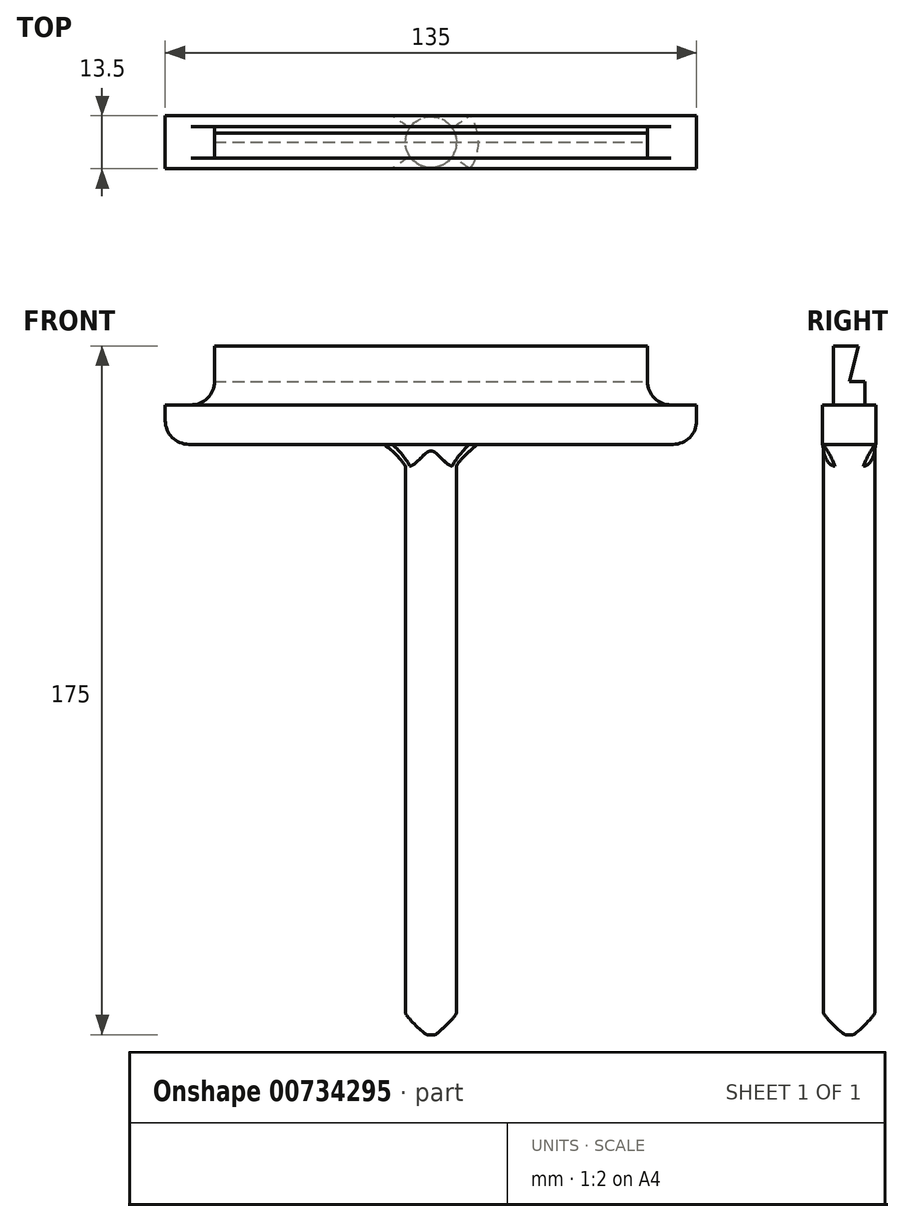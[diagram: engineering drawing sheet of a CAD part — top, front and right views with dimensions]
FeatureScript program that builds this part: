
annotation { "Feature Type Name" : "Feature", "Feature Type Description" : "" }
export const myFeature = defineFeature(function(context is Context, id is Id, definition is map)
    precondition{}
    {
        {
            var Q0;
            Q0=qCreatedBy(makeId("Top.planeOp"),FACE);
            var sketch = newSketch(context, id + "F0", { "sketchPlane" : qUnion([Q0])});
            skLineSegment(sketch, "E0.bottom", {"start": v(67.5, -6.75) * mm, "end": v(-67.5, -6.75) * mm});
            skLineSegment(sketch, "E0.top", {"start": v(67.5, 6.75) * mm, "end": v(-67.5, 6.75) * mm});
            skLineSegment(sketch, "E0.left", {"start": v(67.5, -6.75) * mm, "end": v(67.5, 6.75) * mm});
            skLineSegment(sketch, "E0.right", {"start": v(-67.5, -6.75) * mm, "end": v(-67.5, 6.75) * mm});
            skPoint(sketch, "E0.middle", {"position": v(0, 0) * mm});
            skSolve(sketch);
        }
        {
            var Q0;
            Q0 = qSketchRegion(id + "F0", true);
            extrude(context, id + "F1", {"entities" : qUnion([Q0]), "depth" : 25 * mm, "offsetDistance" : 25 * mm});
        }
        {
            var Q0;
            Q0=makeQuery(id+"F1.opExtrude","CAP_FACE",FACE,{"disambiguationData":[OSD([sQuery(id+"F0.wireOp",EDGE,"E0.bottom"),sQuery(id+"F0.wireOp",EDGE,"E0.top"),sQuery(id+"F0.wireOp",EDGE,"E0.left"),sQuery(id+"F0.wireOp",EDGE,"E0.right")])],"isStart":false});
            var sketch = newSketch(context, id + "F2", { "sketchPlane" : qUnion([Q0])});
            skLineSegment(sketch, "E1.bottom", {"start": v(55, -4) * mm, "end": v(-55, -4) * mm});
            skLineSegment(sketch, "E1.top", {"start": v(55, 4) * mm, "end": v(-55, 4) * mm});
            skLineSegment(sketch, "E1.left", {"start": v(55, -4) * mm, "end": v(55, 4) * mm});
            skLineSegment(sketch, "E1.right", {"start": v(-55, -4) * mm, "end": v(-55, 4) * mm});
            skPoint(sketch, "E1.middle", {"position": v(0, 0) * mm});
            skLineSegment(sketch, "E2.bottom", {"start": v(67.5, -6.75) * mm, "end": v(-67.5, -6.75) * mm});
            skLineSegment(sketch, "E2.top", {"start": v(67.5, 6.75) * mm, "end": v(-67.5, 6.75) * mm});
            skLineSegment(sketch, "E2.left", {"start": v(67.5, -6.75) * mm, "end": v(67.5, 6.75) * mm});
            skLineSegment(sketch, "E2.right", {"start": v(-67.5, -6.75) * mm, "end": v(-67.5, 6.75) * mm});
            skSolve(sketch);
        }
        {
            var Q0;
            Q0 = qSketchRegion(id + "F2", true);
            extrude(context, id + "F3", {"entities" : qUnion([Q0]), "operationType" : NewBodyOperationType.REMOVE, "oppositeDirection" : true, "depth" : 15 * mm, "offsetDistance" : 25 * mm});
        }
        {
            var Q0;
            Q0=makeQuery(id+"F1.opExtrude","CAP_FACE",FACE,{"disambiguationData":[OSD([sQuery(id+"F0.wireOp",EDGE,"E0.bottom"),sQuery(id+"F0.wireOp",EDGE,"E0.top"),sQuery(id+"F0.wireOp",EDGE,"E0.left"),sQuery(id+"F0.wireOp",EDGE,"E0.right")])],"isStart":true});
            var sketch = newSketch(context, id + "F4", { "sketchPlane" : qUnion([Q0])});
            skCircle(sketch, "E3", {"center": v(0, 0) * mm, "radius": 6.5 * mm});
            skSolve(sketch);
        }
        {
            var Q0;
            Q0 = qSketchRegion(id + "F4", true);
            extrude(context, id + "F5", {"entities" : qUnion([Q0]), "operationType" : NewBodyOperationType.ADD, "depth" : 150 * mm, "offsetDistance" : 25 * mm});
        }
        {
            var Q0;
            Q0=makeQuery(id+"F3.boolean.opBoolean","COPY",EDGE,{"derivedFrom":makeQuery(id+"F3.opExtrude","CAP_EDGE",EDGE,{"disambiguationData":[OSD([sQuery(id+"F2.wireOp",EDGE,"E1.right")])],"isStart":true})});
            var Q1;
            Q1=makeQuery(id+"F3.boolean.opBoolean","COPY",EDGE,{"derivedFrom":makeQuery(id+"F3.opExtrude","CAP_EDGE",EDGE,{"disambiguationData":[OSD([sQuery(id+"F2.wireOp",EDGE,"E2.right")])],"isStart":false})});
            var Q2;
            Q2=makeQuery(id+"F1.opExtrude","CAP_EDGE",EDGE,{"disambiguationData":[OSD([sQuery(id+"F0.wireOp",EDGE,"E0.right")])],"isStart":true});
            var Q3;
            Q3=makeQuery(id+"F3.boolean.opBoolean","COPY",EDGE,{"derivedFrom":makeQuery(id+"F3.opExtrude","CAP_EDGE",EDGE,{"disambiguationData":[OSD([sQuery(id+"F2.wireOp",EDGE,"E1.left")])],"isStart":true})});
            var Q4;
            Q4=makeQuery(id+"F3.boolean.opBoolean","COPY",EDGE,{"derivedFrom":makeQuery(id+"F3.opExtrude","CAP_EDGE",EDGE,{"disambiguationData":[OSD([sQuery(id+"F2.wireOp",EDGE,"E2.left")])],"isStart":false})});
            var Q5;
            Q5=makeQuery(id+"F1.opExtrude","CAP_EDGE",EDGE,{"disambiguationData":[OSD([sQuery(id+"F0.wireOp",EDGE,"E0.left")])],"isStart":true});
            var Q6;
            Q6=makeQuery(id+"F3.boolean.opBoolean","COPY",EDGE,{"derivedFrom":makeQuery(id+"F3.opExtrude","CAP_EDGE",EDGE,{"disambiguationData":[OSD([sQuery(id+"F2.wireOp",EDGE,"E1.right")])],"isStart":false})});
            var Q7;
            Q7=makeQuery(id+"F3.boolean.opBoolean","COPY",EDGE,{"derivedFrom":makeQuery(id+"F3.opExtrude","CAP_EDGE",EDGE,{"disambiguationData":[OSD([sQuery(id+"F2.wireOp",EDGE,"E1.left")])],"isStart":false})});
            fillet(context, id + "F6", {"entities" : qUnion([Q0, Q1, Q2, Q3, Q4, Q5, Q6, Q7]), "radius" : 6 * mm, "tangentPropagation" : true, "allowEdgeOverflow" : false});
        }
        {
            var Q0;
            Q0=makeQuery(id+"F3.boolean.opBoolean","COPY",FACE,{"derivedFrom":makeQuery(id+"F3.opExtrude","SWEPT_FACE",FACE,{"disambiguationData":[OSD([sQuery(id+"F2.wireOp",EDGE,"E1.left")])]})});
            var sketch = newSketch(context, id + "F7", { "sketchPlane" : qUnion([Q0])});
            skLineSegment(sketch, "E4", {"start": v(0, 16) * mm, "end": v(2.32, 25) * mm});
            skLineSegment(sketch, "E5", {"start": v(2.32, 25) * mm, "end": v(4.02, 25) * mm});
            skLineSegment(sketch, "E6", {"start": v(4.02, 25) * mm, "end": v(4, 16) * mm});
            skLineSegment(sketch, "E7", {"start": v(4, 16) * mm, "end": v(0, 16) * mm});
            skSolve(sketch);
        }
        {
            var Q0;
            Q0 = qSketchRegion(id + "F7", true);
            extrude(context, id + "F8", {"entities" : qUnion([Q0]), "operationType" : NewBodyOperationType.REMOVE, "oppositeDirection" : true, "depth" : 150 * mm, "offsetDistance" : 25 * mm});
        }
        {
            var Q0;
            Q0=makeQuery(id+"F5.opExtrude","CAP_EDGE",EDGE,{"disambiguationData":[OSD([sQuery(id+"F4.wireOp",EDGE,"E3")])],"isStart":false});
            var Q1;
            Q1=makeQuery(id+"F5.opExtrude","SWEPT_FACE",FACE,{"disambiguationData":[OSD([sQuery(id+"F4.wireOp",EDGE,"E3")])]});
            fillet(context, id + "F9", {"entities" : qUnion([Q0, Q1]), "radius" : 5.55 * mm, "tangentPropagation" : true, "rho" : 0.1, "crossSection" : FilletCrossSection.CONIC, "allowEdgeOverflow" : false});
        }
    });
